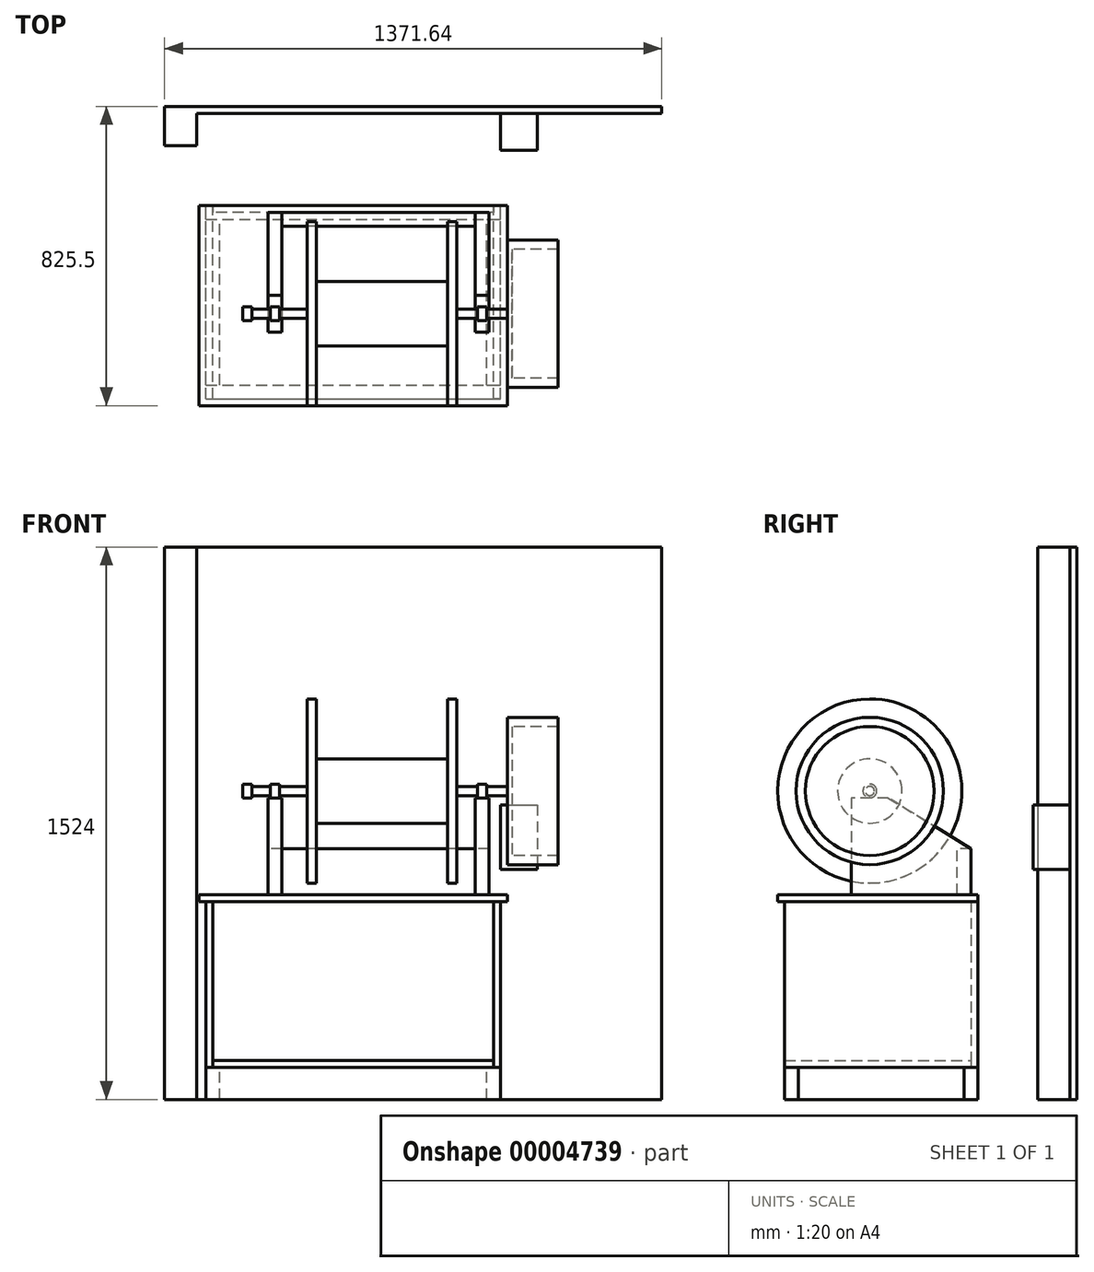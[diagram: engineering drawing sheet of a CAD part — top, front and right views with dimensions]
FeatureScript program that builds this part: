
annotation { "Feature Type Name" : "Feature", "Feature Type Description" : "" }
export const myFeature = defineFeature(function(context is Context, id is Id, definition is map)
    precondition{}
    {
        {
            var Q0;
            Q0=qCreatedBy(makeId("Front.planeOp"),FACE);
            var sketch = newSketch(context, id + "F0", { "sketchPlane" : qUnion([Q0])});
            skLineSegment(sketch, "E0.bottom", {"start": v(0, 0) * mm, "end": v(812.8, 0) * mm});
            skLineSegment(sketch, "E0.top", {"start": v(0, 88.9) * mm, "end": v(812.8, 88.9) * mm});
            skLineSegment(sketch, "E0.left", {"start": v(0, 0) * mm, "end": v(0, 88.9) * mm});
            skLineSegment(sketch, "E0.right", {"start": v(812.8, 0) * mm, "end": v(812.8, 88.9) * mm});
            skSolve(sketch);
        }
        {
            var Q0;
            Q0 = qSketchRegion(id + "F0", true);
            extrude(context, id + "F1", {"entities" : qUnion([Q0]), "depth" : 38.1 * mm});
        }
        {
            var Q0;
            Q0=makeQuery(id+"F1.opExtrude","CAP_FACE",FACE,{"disambiguationData":[OSD([sQuery(id+"F0.wireOp",EDGE,"E0.bottom"),sQuery(id+"F0.wireOp",EDGE,"E0.top"),sQuery(id+"F0.wireOp",EDGE,"E0.left"),sQuery(id+"F0.wireOp",EDGE,"E0.right")])],"isStart":false});
            var sketch = newSketch(context, id + "F2", { "sketchPlane" : qUnion([Q0])});
            skLineSegment(sketch, "E1.bottom", {"start": v(0, 0) * mm, "end": v(38.1, 0) * mm});
            skLineSegment(sketch, "E1.top", {"start": v(0, 88.9) * mm, "end": v(38.1, 88.9) * mm});
            skLineSegment(sketch, "E1.left", {"start": v(0, 0) * mm, "end": v(0, 88.9) * mm});
            skLineSegment(sketch, "E1.right", {"start": v(38.1, 0) * mm, "end": v(38.1, 88.9) * mm});
            skLineSegment(sketch, "E2.bottom", {"start": v(812.8, 0) * mm, "end": v(774.7, 0) * mm});
            skLineSegment(sketch, "E2.top", {"start": v(812.8, 88.9) * mm, "end": v(774.7, 88.9) * mm});
            skLineSegment(sketch, "E2.left", {"start": v(812.8, 0) * mm, "end": v(812.8, 88.9) * mm});
            skLineSegment(sketch, "E2.right", {"start": v(774.7, 0) * mm, "end": v(774.7, 88.9) * mm});
            skSolve(sketch);
        }
        {
            var Q0;
            Q0 = qSketchRegion(id + "F2", true);
            extrude(context, id + "F3", {"entities" : qUnion([Q0]), "depth" : 457.2 * mm});
        }
        {
            var Q0;
            Q0=makeQuery(id+"F3.opExtrude","CAP_FACE",FACE,{"disambiguationData":[OSD([sQuery(id+"F2.wireOp",EDGE,"E1.bottom"),sQuery(id+"F2.wireOp",EDGE,"E1.top"),sQuery(id+"F2.wireOp",EDGE,"E1.left"),sQuery(id+"F2.wireOp",EDGE,"E1.right")])],"isStart":false});
            var sketch = newSketch(context, id + "F4", { "sketchPlane" : qUnion([Q0])});
            skLineSegment(sketch, "E3.bottom", {"start": v(0, 0) * mm, "end": v(812.8, 0) * mm});
            skLineSegment(sketch, "E3.top", {"start": v(0, 88.9) * mm, "end": v(812.8, 88.9) * mm});
            skLineSegment(sketch, "E3.left", {"start": v(0, 0) * mm, "end": v(0, 88.9) * mm});
            skLineSegment(sketch, "E3.right", {"start": v(812.8, 0) * mm, "end": v(812.8, 88.9) * mm});
            skSolve(sketch);
        }
        {
            var Q0;
            Q0 = qSketchRegion(id + "F4", true);
            extrude(context, id + "F5", {"entities" : qUnion([Q0]), "depth" : 38.1 * mm});
        }
        {
            var Q0;
            Q0=makeQuery(id+"F5.boolean.opBoolean","MERGE",FACE,{"derivedFrom":[makeQuery(id+"F3.boolean.opBoolean","MERGE",FACE,{"derivedFrom":[makeQuery(id+"F1.opExtrude","SWEPT_FACE",FACE,{"disambiguationData":[OSD([sQuery(id+"F0.wireOp",EDGE,"E0.top")])]}),makeQuery(id+"F3.opExtrude","SWEPT_FACE",FACE,{"disambiguationData":[OSD([sQuery(id+"F2.wireOp",EDGE,"E1.top")])]}),makeQuery(id+"F3.opExtrude","SWEPT_FACE",FACE,{"disambiguationData":[OSD([sQuery(id+"F2.wireOp",EDGE,"E2.top")])]})]}),makeQuery(id+"F5.opExtrude","SWEPT_FACE",FACE,{"disambiguationData":[OSD([sQuery(id+"F4.wireOp",EDGE,"E3.top")])]})]});
            var sketch = newSketch(context, id + "F6", { "sketchPlane" : qUnion([Q0])});
            skLineSegment(sketch, "E4.bottom", {"start": v(0, -533.4) * mm, "end": v(19.05, -533.4) * mm});
            skLineSegment(sketch, "E4.top", {"start": v(0, 0) * mm, "end": v(19.05, 0) * mm});
            skLineSegment(sketch, "E4.left", {"start": v(0, -533.4) * mm, "end": v(0, 0) * mm});
            skLineSegment(sketch, "E4.right", {"start": v(19.05, -533.4) * mm, "end": v(19.05, 0) * mm});
            skLineSegment(sketch, "E5.bottom", {"start": v(812.8, -533.4) * mm, "end": v(793.75, -533.4) * mm});
            skLineSegment(sketch, "E5.top", {"start": v(812.8, 0) * mm, "end": v(793.75, 0) * mm});
            skLineSegment(sketch, "E5.left", {"start": v(812.8, -533.4) * mm, "end": v(812.8, 0) * mm});
            skLineSegment(sketch, "E5.right", {"start": v(793.75, -533.4) * mm, "end": v(793.75, 0) * mm});
            skSolve(sketch);
        }
        {
            var Q0;
            Q0 = qSketchRegion(id + "F6", true);
            extrude(context, id + "F7", {"entities" : qUnion([Q0]), "depth" : 457.2 * mm});
        }
        {
            var Q0;
            Q0=makeQuery(id+"F7.opExtrude","CAP_FACE",FACE,{"disambiguationData":[OSD([sQuery(id+"F6.wireOp",EDGE,"E4.bottom"),sQuery(id+"F6.wireOp",EDGE,"E4.top"),sQuery(id+"F6.wireOp",EDGE,"E4.left"),sQuery(id+"F6.wireOp",EDGE,"E4.right")])],"isStart":false});
            var sketch = newSketch(context, id + "F8", { "sketchPlane" : qUnion([Q0])});
            skLineSegment(sketch, "E6.bottom", {"start": v(-19.05, -552.45) * mm, "end": v(831.85, -552.45) * mm});
            skLineSegment(sketch, "E6.top", {"start": v(-19.05, 0) * mm, "end": v(831.85, 0) * mm});
            skLineSegment(sketch, "E6.left", {"start": v(-19.05, -552.45) * mm, "end": v(-19.05, 0) * mm});
            skLineSegment(sketch, "E6.right", {"start": v(831.85, -552.45) * mm, "end": v(831.85, 0) * mm});
            skSolve(sketch);
        }
        {
            var Q0;
            Q0 = qSketchRegion(id + "F8", true);
            extrude(context, id + "F9", {"entities" : qUnion([Q0]), "depth" : 19.05 * mm});
        }
        {
            var Q0;
            Q0=makeQuery(id+"F5.opExtrude","SWEPT_FACE",FACE,{"disambiguationData":[OSD([sQuery(id+"F4.wireOp",EDGE,"E3.top")])]});
            var sketch = newSketch(context, id + "F10", { "sketchPlane" : qUnion([Q0])});
            skLineSegment(sketch, "E7.bottom", {"start": v(19.05, -533.4) * mm, "end": v(793.75, -533.4) * mm});
            skLineSegment(sketch, "E7.top", {"start": v(19.05, -19.05) * mm, "end": v(793.75, -19.05) * mm});
            skLineSegment(sketch, "E7.left", {"start": v(19.05, -533.4) * mm, "end": v(19.05, -19.05) * mm});
            skLineSegment(sketch, "E7.right", {"start": v(793.75, -533.4) * mm, "end": v(793.75, -19.05) * mm});
            skSolve(sketch);
        }
        {
            var Q0;
            Q0 = qSketchRegion(id + "F10", true);
            extrude(context, id + "F11", {"entities" : qUnion([Q0]), "depth" : 19.05 * mm});
        }
        {
            var Q0;
            Q0=makeQuery(id+"F1.opExtrude","SWEPT_FACE",FACE,{"disambiguationData":[OSD([sQuery(id+"F0.wireOp",EDGE,"E0.top")])]});
            var sketch = newSketch(context, id + "F12", { "sketchPlane" : qUnion([Q0])});
            skLineSegment(sketch, "E8.bottom", {"start": v(793.75, 0) * mm, "end": v(19.05, 0) * mm});
            skLineSegment(sketch, "E8.top", {"start": v(793.75, -19.05) * mm, "end": v(19.05, -19.05) * mm});
            skLineSegment(sketch, "E8.left", {"start": v(793.75, 0) * mm, "end": v(793.75, -19.05) * mm});
            skLineSegment(sketch, "E8.right", {"start": v(19.05, 0) * mm, "end": v(19.05, -19.05) * mm});
            skSolve(sketch);
        }
        {
            var Q0;
            Q0 = qSketchRegion(id + "F12", true);
            extrude(context, id + "F13", {"entities" : qUnion([Q0]), "endBound" : BoundingType.UP_TO_NEXT, "depth" : 25.4 * mm});
        }
        {
            var Q0;
            Q0=makeQuery(id+"F9.opExtrude","CAP_FACE",FACE,{"disambiguationData":[OSD([sQuery(id+"F8.wireOp",EDGE,"E6.bottom"),sQuery(id+"F8.wireOp",EDGE,"E6.top"),sQuery(id+"F8.wireOp",EDGE,"E6.left"),sQuery(id+"F8.wireOp",EDGE,"E6.right")])],"isStart":false});
            var sketch = newSketch(context, id + "F14", { "sketchPlane" : qUnion([Q0])});
            skLineSegment(sketch, "E9.bottom", {"start": v(171.45, -19.05) * mm, "end": v(209.55, -19.05) * mm});
            skLineSegment(sketch, "E9.top", {"start": v(171.45, -349.25) * mm, "end": v(209.55, -349.25) * mm});
            skLineSegment(sketch, "E9.left", {"start": v(171.45, -19.05) * mm, "end": v(171.45, -349.25) * mm});
            skLineSegment(sketch, "E9.right", {"start": v(209.55, -19.05) * mm, "end": v(209.55, -349.25) * mm});
            skLineSegment(sketch, "E10.bottom", {"start": v(781.05, -19.05) * mm, "end": v(742.95, -19.05) * mm});
            skLineSegment(sketch, "E10.top", {"start": v(781.05, -349.25) * mm, "end": v(742.95, -349.25) * mm});
            skLineSegment(sketch, "E10.left", {"start": v(781.05, -19.05) * mm, "end": v(781.05, -349.25) * mm});
            skLineSegment(sketch, "E10.right", {"start": v(742.95, -19.05) * mm, "end": v(742.95, -349.25) * mm});
            skLineSegment(sketch, "E11", {"start": v(190.5, -19.05) * mm, "end": v(190.5, -349.25) * mm, "construction": true});
            skLineSegment(sketch, "E12", {"start": v(762, -19.05) * mm, "end": v(762, -349.25) * mm, "construction": true});
            skLineSegment(sketch, "E13", {"start": v(406.4, -552.45) * mm, "end": v(406.4, -298.45) * mm, "construction": true});
            skSolve(sketch);
        }
        {
            var Q0;
            Q0 = qSketchRegion(id + "F14", true);
            extrude(context, id + "F15", {"entities" : qUnion([Q0]), "depth" : 266.7 * mm});
        }
        {
            var Q0;
            Q0=makeQuery(id+"F15.opExtrude","SWEPT_FACE",FACE,{"disambiguationData":[OSD([sQuery(id+"F14.wireOp",EDGE,"E9.left")])]});
            var sketch = newSketch(context, id + "F16", { "sketchPlane" : qUnion([Q0])});
            skLineSegment(sketch, "E14", {"start": v(19.05, 692.15) * mm, "end": v(247.65, 831.85) * mm});
            skLineSegment(sketch, "E15", {"start": v(247.65, 831.85) * mm, "end": v(19.05, 831.85) * mm});
            skLineSegment(sketch, "E16", {"start": v(19.05, 831.85) * mm, "end": v(19.05, 692.15) * mm});
            skSolve(sketch);
        }
        {
            var Q0;
            Q0 = qSketchRegion(id + "F16", true);
            extrude(context, id + "F17", {"entities" : qUnion([Q0]), "operationType" : NewBodyOperationType.REMOVE, "endBound" : BoundingType.THROUGH_ALL, "oppositeDirection" : true, "depth" : 25.4 * mm});
        }
        {
            var Q0;
            Q0=qCreatedBy(makeId("Top.planeOp"),FACE);
            var sketch = newSketch(context, id + "F18", { "sketchPlane" : qUnion([Q0])});
            skLineSegment(sketch, "E17.bottom", {"start": v(-25.4, 254) * mm, "end": v(-114.3, 254) * mm});
            skLineSegment(sketch, "E17.top", {"start": v(-25.4, 165.1) * mm, "end": v(-114.3, 165.1) * mm});
            skLineSegment(sketch, "E17.left", {"start": v(-25.4, 254) * mm, "end": v(-25.4, 165.1) * mm});
            skLineSegment(sketch, "E17.right", {"start": v(-114.3, 254) * mm, "end": v(-114.3, 165.1) * mm});
            skSolve(sketch);
        }
        {
            var Q0;
            Q0 = qSketchRegion(id + "F18", true);
            extrude(context, id + "F19", {"entities" : qUnion([Q0]), "depth" : 1524 * mm});
        }
        {
            var Q0;
            Q0=makeQuery(id+"F15.opExtrude","SWEPT_FACE",FACE,{"disambiguationData":[OSD([sQuery(id+"F14.wireOp",EDGE,"E9.right")])]});
            var sketch = newSketch(context, id + "F20", { "sketchPlane" : qUnion([Q0])});
            skLineSegment(sketch, "E18.bottom", {"start": v(-19.05, 565.15) * mm, "end": v(-57.15, 565.15) * mm});
            skLineSegment(sketch, "E18.top", {"start": v(-19.05, 692.15) * mm, "end": v(-57.15, 692.15) * mm});
            skLineSegment(sketch, "E18.left", {"start": v(-19.05, 565.15) * mm, "end": v(-19.05, 692.15) * mm});
            skLineSegment(sketch, "E18.right", {"start": v(-57.15, 565.15) * mm, "end": v(-57.15, 692.15) * mm});
            skSolve(sketch);
        }
        {
            var Q0;
            Q0 = qSketchRegion(id + "F20", true);
            extrude(context, id + "F21", {"entities" : qUnion([Q0]), "endBound" : BoundingType.UP_TO_NEXT, "depth" : 25.4 * mm});
        }
        {
            var Q0;
            Q0=makeQuery(id+"F19.opExtrude","SWEPT_FACE",FACE,{"disambiguationData":[OSD([sQuery(id+"F18.wireOp",EDGE,"E17.bottom")])]});
            var sketch = newSketch(context, id + "F22", { "sketchPlane" : qUnion([Q0])});
            skLineSegment(sketch, "E19.bottom", {"start": v(114.3, 0) * mm, "end": v(-1257.34, 0) * mm});
            skLineSegment(sketch, "E19.top", {"start": v(114.3, 1524) * mm, "end": v(-1257.34, 1524) * mm});
            skLineSegment(sketch, "E19.left", {"start": v(114.3, 0) * mm, "end": v(114.3, 1524) * mm});
            skLineSegment(sketch, "E19.right", {"start": v(-1257.34, 0) * mm, "end": v(-1257.34, 1524) * mm});
            skSolve(sketch);
        }
        {
            var Q0;
            Q0 = qSketchRegion(id + "F22", true);
            extrude(context, id + "F23", {"entities" : qUnion([Q0]), "operationType" : NewBodyOperationType.ADD, "depth" : 19.05 * mm});
        }
        {
            var Q0;
            Q0=makeQuery(id+"F23.opExtrude","CAP_FACE",FACE,{"disambiguationData":[OSD([sQuery(id+"F22.wireOp",EDGE,"E19.bottom"),sQuery(id+"F22.wireOp",EDGE,"E19.top"),sQuery(id+"F22.wireOp",EDGE,"E19.left"),sQuery(id+"F22.wireOp",EDGE,"E19.right")])],"isStart":true});
            var sketch = newSketch(context, id + "F24", { "sketchPlane" : qUnion([Q0])});
            skLineSegment(sketch, "E20.bottom", {"start": v(812.8, 812.8) * mm, "end": v(914.4, 812.8) * mm});
            skLineSegment(sketch, "E20.top", {"start": v(812.8, 635) * mm, "end": v(914.4, 635) * mm});
            skLineSegment(sketch, "E20.left", {"start": v(812.8, 812.8) * mm, "end": v(812.8, 635) * mm});
            skLineSegment(sketch, "E20.right", {"start": v(914.4, 812.8) * mm, "end": v(914.4, 635) * mm});
            skSolve(sketch);
        }
        {
            var Q0;
            Q0 = qSketchRegion(id + "F24", true);
            extrude(context, id + "F25", {"entities" : qUnion([Q0]), "depth" : 101.6 * mm});
        }
        {
            var Q0;
            Q0=qCreatedBy(makeId("Front.planeOp"),FACE);
            var Q1;
            Q1=sQuery(id+"F14.wireOp",VERTEX,"E13.end");
            cPlane(context, id + "F26", {"entities" : qUnion([Q0, Q1]), "cplaneType" : CPlaneType.PLANE_POINT, "offset" : 152.4 * mm, "width" : 152.4 * mm, "height" : 152.4 * mm});
        }
        {
            var Q0;
            Q0=qCreatedBy(id+"F26.planeOp",FACE);
            var sketch = newSketch(context, id + "F27", { "sketchPlane" : qUnion([Q0])});
            skLineSegment(sketch, "E21", {"start": v(-52.96, 850.9) * mm, "end": v(924.82, 850.9) * mm, "construction": true});
            skLineSegment(sketch, "E22", {"start": v(101.6, 850.9) * mm, "end": v(101.6, 869.95) * mm});
            skLineSegment(sketch, "E23", {"start": v(101.6, 869.95) * mm, "end": v(127, 869.95) * mm});
            skLineSegment(sketch, "E24", {"start": v(127, 869.95) * mm, "end": v(127, 863.6) * mm});
            skLineSegment(sketch, "E25", {"start": v(279.4, 863.6) * mm, "end": v(279.4, 1104.9) * mm});
            skLineSegment(sketch, "E26", {"start": v(279.4, 1104.9) * mm, "end": v(304.8, 1104.9) * mm});
            skLineSegment(sketch, "E27", {"start": v(304.8, 1104.9) * mm, "end": v(304.8, 939.8) * mm});
            skLineSegment(sketch, "E28", {"start": v(666.75, 939.8) * mm, "end": v(666.75, 1104.9) * mm});
            skLineSegment(sketch, "E29", {"start": v(666.75, 1104.9) * mm, "end": v(692.15, 1104.9) * mm});
            skLineSegment(sketch, "E30", {"start": v(692.15, 1104.9) * mm, "end": v(692.15, 863.6) * mm});
            skLineSegment(sketch, "E31", {"start": v(831.85, 863.6) * mm, "end": v(831.85, 1054.1) * mm});
            skLineSegment(sketch, "E32", {"start": v(831.85, 1054.1) * mm, "end": v(971.55, 1054.1) * mm});
            skLineSegment(sketch, "E33", {"start": v(971.55, 1054.1) * mm, "end": v(971.55, 1028.7) * mm});
            skLineSegment(sketch, "E34", {"start": v(971.55, 1028.7) * mm, "end": v(844.55, 1028.7) * mm});
            skLineSegment(sketch, "E35", {"start": v(844.55, 1028.7) * mm, "end": v(844.55, 850.9) * mm});
            skLineSegment(sketch, "E36", {"start": v(844.55, 850.9) * mm, "end": v(101.6, 850.9) * mm});
            skLineSegment(sketch, "E37", {"start": v(304.8, 939.8) * mm, "end": v(666.75, 939.8) * mm});
            skPoint(sketch, "E38", {"position": v(485.77, 939.8) * mm});
            skLineSegment(sketch, "E39", {"start": v(177.8, 863.6) * mm, "end": v(177.8, 869.95) * mm});
            skLineSegment(sketch, "E40", {"start": v(177.8, 869.95) * mm, "end": v(203.2, 869.95) * mm});
            skLineSegment(sketch, "E41", {"start": v(203.2, 869.95) * mm, "end": v(203.2, 863.6) * mm});
            skLineSegment(sketch, "E42", {"start": v(127, 863.6) * mm, "end": v(177.8, 863.6) * mm});
            skLineSegment(sketch, "E43", {"start": v(203.2, 863.6) * mm, "end": v(279.4, 863.6) * mm});
            skLineSegment(sketch, "E44", {"start": v(749.3, 863.6) * mm, "end": v(749.3, 869.95) * mm});
            skLineSegment(sketch, "E45", {"start": v(749.3, 869.95) * mm, "end": v(774.7, 869.95) * mm});
            skLineSegment(sketch, "E46", {"start": v(774.7, 869.95) * mm, "end": v(774.7, 863.6) * mm});
            skLineSegment(sketch, "E47", {"start": v(692.15, 863.6) * mm, "end": v(749.3, 863.6) * mm});
            skLineSegment(sketch, "E48", {"start": v(774.7, 863.6) * mm, "end": v(831.85, 863.6) * mm});
            skPoint(sketch, "E49", {"position": v(190.5, 869.95) * mm});
            skPoint(sketch, "E50", {"position": v(762, 869.95) * mm});
            skSolve(sketch);
        }
        {
            var Q0;
            Q0 = qSketchRegion(id + "F27", true);
            var Q1;
            Q1=sQuery(id+"F27.wireOp",EDGE,"E21");
            revolve(context, id + "F28", {"entities" : qUnion([Q0]), "axis" : qUnion([Q1]), "revolveType" : RevolveType.FULL});
        }
    });
